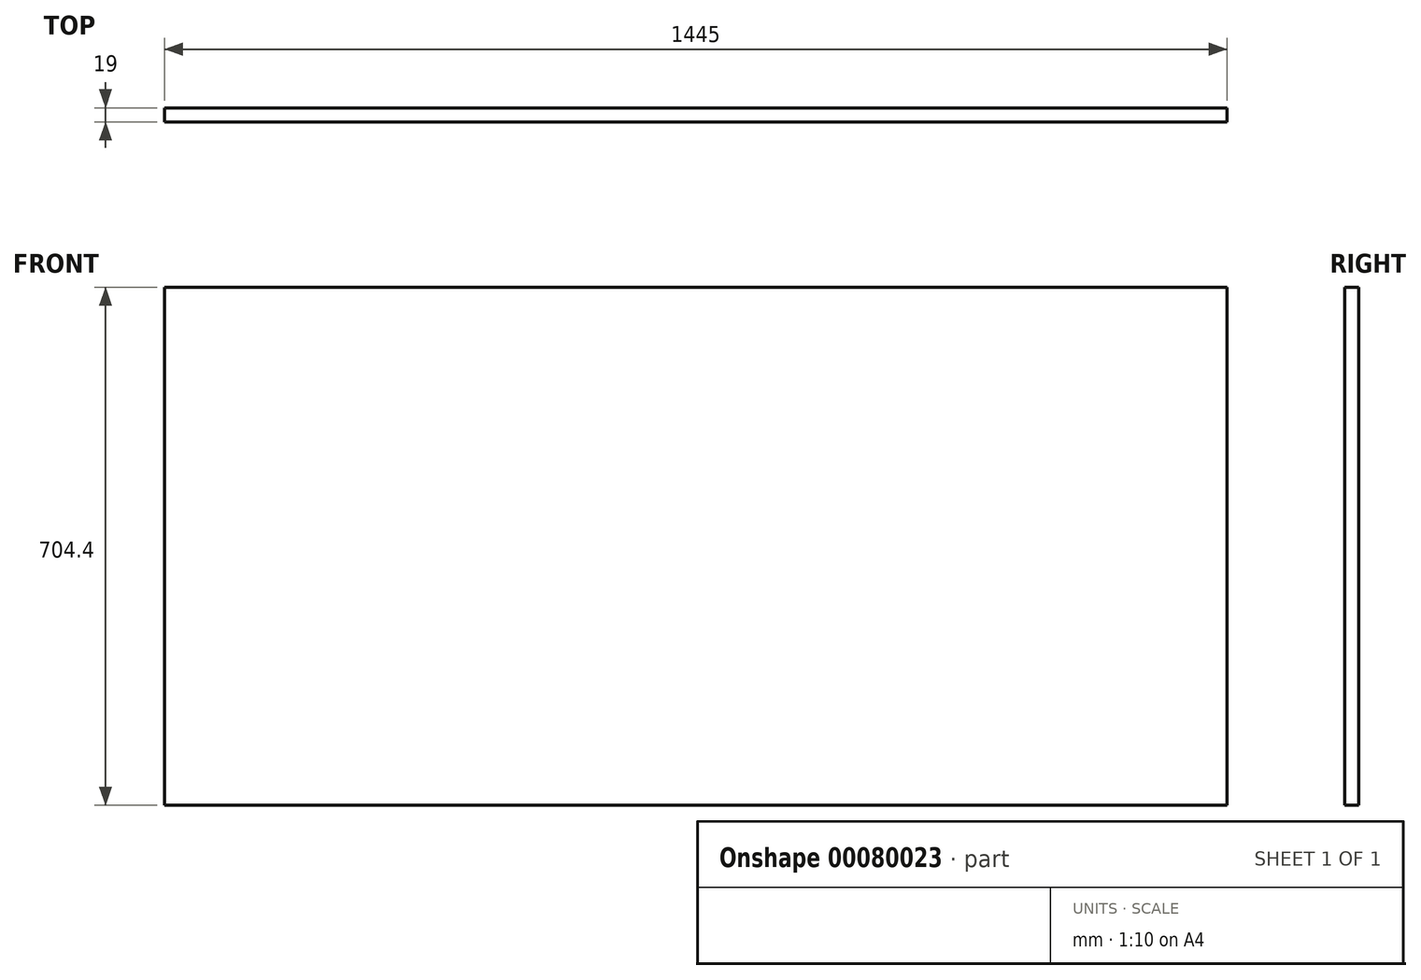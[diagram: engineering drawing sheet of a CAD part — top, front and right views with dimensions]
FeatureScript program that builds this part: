
annotation { "Feature Type Name" : "Feature", "Feature Type Description" : "" }
export const myFeature = defineFeature(function(context is Context, id is Id, definition is map)
    precondition{}
    {
        {
            var Q0;
            Q0=qCreatedBy(makeId("Front.planeOp"),FACE);
            var sketch = newSketch(context, id + "F0", { "sketchPlane" : qUnion([Q0])});
            skLineSegment(sketch, "E0.bottom", {"start": v(0, 0) * mm, "end": v(1445, 0) * mm});
            skLineSegment(sketch, "E0.top", {"start": v(0, -704.4) * mm, "end": v(1445, -704.4) * mm});
            skLineSegment(sketch, "E0.left", {"start": v(0, 0) * mm, "end": v(0, -704.4) * mm});
            skLineSegment(sketch, "E0.right", {"start": v(1445, 0) * mm, "end": v(1445, -704.4) * mm});
            skSolve(sketch);
        }
        {
            var Q0;
            Q0=makeQuery(id+"F0.imprint","IMPRINT",FACE,{"disambiguationData":[TD([[makeQuery(id+"F0.imprint","IMPRINT",EDGE,{"derivedFrom":sQuery(id+"F0.wireOp",EDGE,"E0.bottom")}),-1.0]])]});
            extrude(context, id + "F1", {"entities" : qUnion([Q0]), "depth" : 19 * mm});
        }
    });
